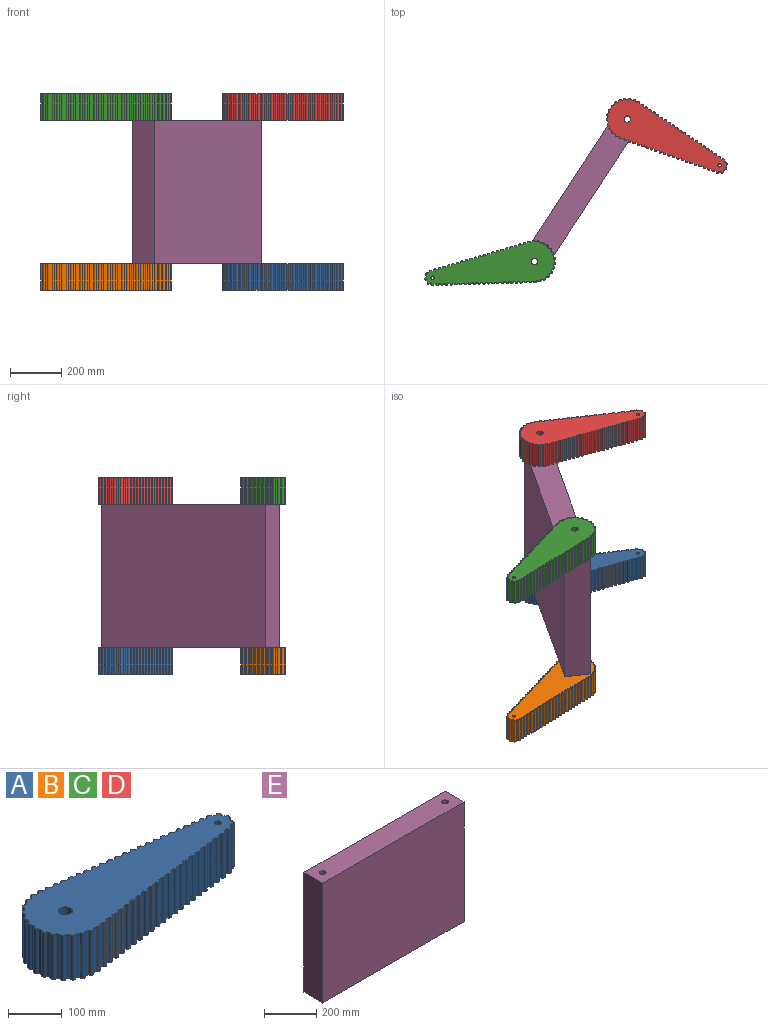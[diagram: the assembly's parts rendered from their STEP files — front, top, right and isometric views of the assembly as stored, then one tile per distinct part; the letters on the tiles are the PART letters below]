
ASSEMBLY  parts=5 mates=10
PART A: 128 faces, bbox 512.4x161.4x101.6 mm
  f0: plane 101.6x8.01mm, normal (0.13,-0.99,0), area 820.8mm2, adj f1,f124,f126,f127
  f1: cylinder r=5mm len=101.6mm, axis (0,0,-1), area 1595.9mm2, adj f0,f2,f126,f127
  f2: plane 101.6x8.01mm, normal (0.13,-0.99,0), area 820.8mm2, adj f1,f3,f126,f127
  f3: cylinder r=5mm len=101.6mm, axis (0,0,-1), area 1595.9mm2, adj f2,f4,f126,f127
  f4: plane 101.6x8.01mm, normal (0.13,-0.99,0), area 820.8mm2, adj f3,f5,f126,f127
  f5: cylinder r=5mm len=101.6mm, axis (0,0,-1), area 1595.9mm2, adj f4,f6,f126,f127
  f6: plane 101.6x8.01mm, normal (0.13,-0.99,0), area 820.8mm2, adj f5,f7,f126,f127
  f7: cylinder r=5mm len=101.6mm, axis (0,0,-1), area 1595.9mm2, adj f6,f8,f126,f127
  f8: plane 101.6x8.01mm, normal (0.13,-0.99,0), area 820.8mm2, adj f7,f9,f126,f127
  f9: cylinder r=5mm len=101.6mm, axis (0,0,-1), area 1595.9mm2, adj f8,f10,f126,f127
  f10: plane 101.6x8.01mm, normal (0.13,-0.99,0), area 820.8mm2, adj f9,f11,f126,f127
  f11: cylinder r=5mm len=101.6mm, axis (0,0,-1), area 1595.9mm2, adj f10,f12,f126,f127
  f12: plane 101.6x8.01mm, normal (0.13,-0.99,0), area 820.8mm2, adj f11,f13,f126,f127
  f13: cylinder r=5mm len=101.6mm, axis (0,0,-1), area 1595.9mm2, adj f12,f14,f126,f127
  f14: plane 101.6x8.01mm, normal (0.13,-0.99,0), area 820.8mm2, adj f13,f15,f126,f127
  f15: cylinder r=5mm len=101.6mm, axis (0,0,-1), area 1595.9mm2, adj f14,f16,f126,f127
  f16: plane 101.6x8.01mm, normal (0.13,-0.99,0), area 820.8mm2, adj f15,f17,f126,f127
  f17: cylinder r=5mm len=101.6mm, axis (0,0,-1), area 1595.9mm2, adj f16,f18,f126,f127
  f18: plane 101.6x8.01mm, normal (0.13,-0.99,0), area 820.8mm2, adj f17,f19,f126,f127
  f19: cylinder r=5mm len=101.6mm, axis (0,0,-1), area 1595.9mm2, adj f18,f20,f126,f127
  f20: plane 101.6x8.01mm, normal (0.13,-0.99,0), area 820.8mm2, adj f19,f21,f126,f127
  f21: cylinder r=5mm len=101.6mm, axis (0,0,-1), area 1595.9mm2, adj f20,f22,f126,f127
  f22: plane 101.6x8.01mm, normal (0.13,-0.99,0), area 820.8mm2, adj f21,f23,f126,f127
  f23: cylinder r=5mm len=101.6mm, axis (0,0,-1), area 1595.9mm2, adj f22,f24,f126,f127
  f24: plane 101.6x8.01mm, normal (0.13,-0.99,0), area 820.8mm2, adj f23,f25,f126,f127
  f25: cylinder r=5mm len=101.6mm, axis (0,0,-1), area 1595.9mm2, adj f24,f26,f126,f127
  f26: plane 101.6x8.01mm, normal (0.13,-0.99,0), area 820.8mm2, adj f25,f27,f126,f127
  f27: cylinder r=5mm len=101.6mm, axis (0,0,-1), area 1595.9mm2, adj f26,f28,f126,f127
  f28: plane 101.6x8.01mm, normal (0.13,-0.99,0), area 820.8mm2, adj f27,f29,f126,f127
  f29: cylinder r=5mm len=101.6mm, axis (0,0,-1), area 1595.9mm2, adj f28,f30,f126,f127
  f30: plane 101.6x8.01mm, normal (0.13,-0.99,0), area 820.8mm2, adj f29,f31,f126,f127
  f31: cylinder r=5mm len=101.6mm, axis (0,0,-1), area 1595.9mm2, adj f30,f32,f126,f127
  f32: plane 101.6x8.01mm, normal (0.13,-0.99,0), area 820.8mm2, adj f31,f33,f126,f127
  f33: cylinder r=5mm len=101.6mm, axis (0,0,-1), area 1595.9mm2, adj f32,f34,f126,f127
  f34: plane 101.6x8.01mm, normal (0.13,-0.99,0), area 820.8mm2, adj f33,f35,f126,f127
  f35: cylinder r=5mm len=101.6mm, axis (0,0,-1), area 1595.9mm2, adj f34,f36,f126,f127
  f36: plane 101.6x8.01mm, normal (0.13,-0.99,0), area 820.8mm2, adj f35,f37,f126,f127
  f37: cylinder r=5mm len=101.6mm, axis (0,0,-1), area 1595.9mm2, adj f36,f38,f126,f127
  f38: plane 101.6x8.01mm, normal (0.13,-0.99,0), area 820.8mm2, adj f37,f39,f126,f127
  f39: cylinder r=5mm len=101.6mm, axis (0,0,-1), area 1595.9mm2, adj f38,f40,f126,f127
  f40: plane 101.6x8.01mm, normal (0.13,-0.99,0), area 820.8mm2, adj f39,f41,f126,f127
  f41: cylinder r=5mm len=101.6mm, axis (0,0,-1), area 1646.4mm2, adj f40,f42,f126,f127
  f42: cylinder r=25.19mm len=101.6mm, axis (0,0,-1), area 829.1mm2, adj f41,f43,f126,f127
  f43: cylinder r=5mm len=101.6mm, axis (0,0,-1), area 1696.9mm2, adj f42,f44,f126,f127
  f44: cylinder r=25.19mm len=101.6mm, axis (0,0,-1), area 829.1mm2, adj f43,f45,f126,f127
  f45: cylinder r=5mm len=101.6mm, axis (0,0,-1), area 1696.9mm2, adj f44,f46,f126,f127
  f46: cylinder r=25.19mm len=101.6mm, axis (0,0,-1), area 829.1mm2, adj f45,f47,f126,f127
  f47: cylinder r=5mm len=101.6mm, axis (0,0,-1), area 1696.9mm2, adj f46,f48,f126,f127
  f48: cylinder r=25.19mm len=101.6mm, axis (0,0,-1), area 829.1mm2, adj f47,f49,f126,f127
  f49: cylinder r=5mm len=101.6mm, axis (0,0,-1), area 1646.4mm2, adj f48,f50,f126,f127
  f50: plane 101.6x8.01mm, normal (0.13,0.99,0), area 820.8mm2, adj f49,f51,f126,f127
  f51: cylinder r=5mm len=101.6mm, axis (0,0,-1), area 1595.9mm2, adj f50,f52,f126,f127
  f52: plane 101.6x8.01mm, normal (0.13,0.99,0), area 820.8mm2, adj f51,f53,f126,f127
  f53: cylinder r=5mm len=101.6mm, axis (0,0,-1), area 1595.9mm2, adj f52,f54,f126,f127
  f54: plane 101.6x8.01mm, normal (0.13,0.99,0), area 820.8mm2, adj f53,f55,f126,f127
  f55: cylinder r=5mm len=101.6mm, axis (0,0,-1), area 1595.9mm2, adj f54,f56,f126,f127
  f56: plane 101.6x8.01mm, normal (0.13,0.99,0), area 820.8mm2, adj f55,f57,f126,f127
  f57: cylinder r=5mm len=101.6mm, axis (0,0,-1), area 1595.9mm2, adj f56,f58,f126,f127
  f58: plane 101.6x8.01mm, normal (0.13,0.99,0), area 820.8mm2, adj f57,f59,f126,f127
  f59: cylinder r=5mm len=101.6mm, axis (0,0,-1), area 1595.9mm2, adj f58,f60,f126,f127
  f60: plane 101.6x8.01mm, normal (0.13,0.99,0), area 820.8mm2, adj f59,f61,f126,f127
  f61: cylinder r=5mm len=101.6mm, axis (0,0,-1), area 1595.9mm2, adj f60,f62,f126,f127
  f62: plane 101.6x8.01mm, normal (0.13,0.99,0), area 820.8mm2, adj f61,f63,f126,f127
  f63: cylinder r=5mm len=101.6mm, axis (0,0,-1), area 1595.9mm2, adj f62,f64,f126,f127
  f64: plane 101.6x8.01mm, normal (0.13,0.99,0), area 820.8mm2, adj f63,f65,f126,f127
  f65: cylinder r=5mm len=101.6mm, axis (0,0,-1), area 1595.9mm2, adj f64,f66,f126,f127
  f66: plane 101.6x8.01mm, normal (0.13,0.99,0), area 820.8mm2, adj f65,f67,f126,f127
  f67: cylinder r=5mm len=101.6mm, axis (0,0,-1), area 1595.9mm2, adj f66,f68,f126,f127
  f68: plane 101.6x8.01mm, normal (0.13,0.99,0), area 820.8mm2, adj f67,f69,f126,f127
  f69: cylinder r=5mm len=101.6mm, axis (0,0,-1), area 1595.9mm2, adj f68,f70,f126,f127
  f70: plane 101.6x8.01mm, normal (0.13,0.99,0), area 820.8mm2, adj f69,f71,f126,f127
  f71: cylinder r=5mm len=101.6mm, axis (0,0,-1), area 1595.9mm2, adj f70,f72,f126,f127
  f72: plane 101.6x8.01mm, normal (0.13,0.99,0), area 820.8mm2, adj f71,f73,f126,f127
  f73: cylinder r=5mm len=101.6mm, axis (0,0,-1), area 1595.9mm2, adj f72,f74,f126,f127
  f74: plane 101.6x8.01mm, normal (0.13,0.99,0), area 820.8mm2, adj f73,f75,f126,f127
  f75: cylinder r=5mm len=101.6mm, axis (0,0,-1), area 1595.9mm2, adj f74,f76,f126,f127
  f76: plane 101.6x8.01mm, normal (0.13,0.99,0), area 820.8mm2, adj f75,f77,f126,f127
  f77: cylinder r=5mm len=101.6mm, axis (0,0,-1), area 1595.9mm2, adj f76,f78,f126,f127
  f78: plane 101.6x8.01mm, normal (0.13,0.99,0), area 820.8mm2, adj f77,f79,f126,f127
  f79: cylinder r=5mm len=101.6mm, axis (0,0,-1), area 1595.9mm2, adj f78,f80,f126,f127
  f80: plane 101.6x8.01mm, normal (0.13,0.99,0), area 820.8mm2, adj f79,f81,f126,f127
  f81: cylinder r=5mm len=101.6mm, axis (0,0,-1), area 1595.9mm2, adj f80,f82,f126,f127
  f82: plane 101.6x8.01mm, normal (0.13,0.99,0), area 820.8mm2, adj f81,f83,f126,f127
  f83: cylinder r=5mm len=101.6mm, axis (0,0,-1), area 1595.9mm2, adj f82,f84,f126,f127
  f84: plane 101.6x8.01mm, normal (0.13,0.99,0), area 820.8mm2, adj f83,f85,f126,f127
  f85: cylinder r=5mm len=101.6mm, axis (0,0,-1), area 1595.9mm2, adj f84,f86,f126,f127
  f86: plane 101.6x8.01mm, normal (0.13,0.99,0), area 820.8mm2, adj f85,f87,f126,f127
  f87: cylinder r=5mm len=101.6mm, axis (0,0,-1), area 1595.9mm2, adj f86,f88,f126,f127
  f88: plane 101.6x8.01mm, normal (0.13,0.99,0), area 820.8mm2, adj f87,f89,f126,f127
  f89: cylinder r=5mm len=101.6mm, axis (0,0,-1), area 1595.9mm2, adj f88,f90,f126,f127
  f90: plane 101.6x8.01mm, normal (0.13,0.99,0), area 820.8mm2, adj f89,f91,f126,f127
  f91: cylinder r=5mm len=101.6mm, axis (0,0,-1), area 1595.9mm2, adj f90,f92,f126,f127
  f92: plane 101.6x8.01mm, normal (0.13,0.99,0), area 820.8mm2, adj f91,f93,f126,f127
  f93: cylinder r=5mm len=101.6mm, axis (0,0,-1), area 1612.6mm2, adj f92,f94,f126,f127
  f94: cylinder r=76.2mm len=101.6mm, axis (0,0,-1), area 862.2mm2, adj f93,f95,f126,f127
  f95: cylinder r=5mm len=101.6mm, axis (0,0,-1), area 1629.3mm2, adj f94,f96,f126,f127
  f96: cylinder r=76.2mm len=101.6mm, axis (0,0,-1), area 862.2mm2, adj f95,f97,f126,f127
  f97: cylinder r=5mm len=101.6mm, axis (0,0,-1), area 1629.3mm2, adj f96,f98,f126,f127
  f98: cylinder r=76.2mm len=101.6mm, axis (0,0,-1), area 862.2mm2, adj f97,f99,f126,f127
  f99: cylinder r=5mm len=101.6mm, axis (0,0,-1), area 1629.3mm2, adj f98,f100,f126,f127
  f100: cylinder r=76.2mm len=101.6mm, axis (0,0,-1), area 862.2mm2, adj f99,f101,f126,f127
  f101: cylinder r=5mm len=101.6mm, axis (0,0,-1), area 1629.3mm2, adj f100,f102,f126,f127
  f102: cylinder r=76.2mm len=101.6mm, axis (0,0,-1), area 862.2mm2, adj f101,f103,f126,f127
  f103: cylinder r=5mm len=101.6mm, axis (0,0,-1), area 1629.3mm2, adj f102,f104,f126,f127
  f104: cylinder r=76.2mm len=101.6mm, axis (0,0,-1), area 862.2mm2, adj f103,f105,f126,f127
  f105: cylinder r=5mm len=101.6mm, axis (0,0,-1), area 1629.3mm2, adj f104,f106,f126,f127
  f106: cylinder r=76.2mm len=101.6mm, axis (0,0,-1), area 862.2mm2, adj f105,f107,f126,f127
  f107: cylinder r=5mm len=101.6mm, axis (0,0,-1), area 1629.3mm2, adj f106,f108,f126,f127
  f108: cylinder r=76.2mm len=101.6mm, axis (0,0,-1), area 862.2mm2, adj f107,f109,f126,f127
  f109: cylinder r=5mm len=101.6mm, axis (0,0,-1), area 1629.3mm2, adj f108,f110,f126,f127
  f110: cylinder r=76.2mm len=101.6mm, axis (0,0,-1), area 862.2mm2, adj f109,f111,f126,f127
  f111: cylinder r=5mm len=101.6mm, axis (0,0,-1), area 1629.3mm2, adj f110,f112,f126,f127
  f112: cylinder r=76.2mm len=101.6mm, axis (0,0,-1), area 862.2mm2, adj f111,f113,f126,f127
  f113: cylinder r=5mm len=101.6mm, axis (0,0,-1), area 1629.3mm2, adj f112,f114,f126,f127
  f114: cylinder r=76.2mm len=101.6mm, axis (0,0,-1), area 862.2mm2, adj f113,f115,f126,f127
  f115: cylinder r=5mm len=101.6mm, axis (0,0,-1), area 1629.3mm2, adj f114,f116,f126,f127
  f116: cylinder r=76.2mm len=101.6mm, axis (0,0,-1), area 862.2mm2, adj f115,f117,f126,f127
  f117: cylinder r=5mm len=101.6mm, axis (0,0,-1), area 1629.3mm2, adj f116,f118,f126,f127
  f118: cylinder r=76.2mm len=101.6mm, axis (0,0,-1), area 862.2mm2, adj f117,f119,f126,f127
  f119: cylinder r=5mm len=101.6mm, axis (0,0,-1), area 1629.3mm2, adj f118,f120,f126,f127
  f120: cylinder r=76.2mm len=101.6mm, axis (0,0,-1), area 862.2mm2, adj f119,f121,f126,f127
  f121: cylinder r=5mm len=101.6mm, axis (0,0,-1), area 1612.6mm2, adj f120,f122,f126,f127
  f122: plane 101.6x8.01mm, normal (0.13,-0.99,0), area 820.8mm2, adj f121,f124,f126,f127
  f123: cylinder r=6.35mm len=101.6mm, axis (0,0,-1), area 4053.7mm2, adj f126,f127
  f124: cylinder r=5mm len=101.6mm, axis (0,0,-1), area 1595.9mm2, adj f0,f122,f126,f127
  f125: cylinder r=12.7mm len=101.6mm, axis (0,0,-1), area 8107.3mm2, adj f126,f127
  f126: plane 512.38x161.39mm, normal (0,0,1), area 52918.3mm2, adj f0,f1,f2,f3,f4,f5,f6,f7
  f127: plane 512.38x161.39mm, normal (0,0,-1), area 52918.3mm2, adj f0,f1,f2,f3,f4,f5,f6,f7
PART B: same geometry as A
PART C: same geometry as A
PART D: same geometry as A
PART E: 8 faces, bbox 762x101.6x558.8 mm
  f0: plane 558.8x101.6mm, normal (1,0,0), area 56774.1mm2, adj f1,f3,f4,f5
  f1: plane 762x101.6mm, normal (0,0,1), area 76405.8mm2, adj f0,f2,f4,f5,f6,f7
  f2: plane 558.8x101.6mm, normal (-1,0,0), area 56774.1mm2, adj f1,f3,f4,f5
  f3: plane 762x101.6mm, normal (0,0,-1), area 76405.8mm2, adj f0,f2,f4,f5,f6,f7
  f4: plane 762x558.8mm, normal (0,-1,0), area 425805.6mm2, adj f0,f1,f2,f3
  f5: plane 762x558.8mm, normal (0,1,0), area 425805.6mm2, adj f0,f1,f2,f3
  f6: cylinder r=12.7mm len=558.8mm, axis (0,0,1), area 44590.3mm2, adj f1,f3
  f7: cylinder r=12.7mm len=558.8mm, axis (0,0,1), area 44590.3mm2, adj f1,f3
PLACE A rot(axis=(0,0,-1),26.7deg) t=(89.01,614.73,-807.95)mm
PLACE B rot(axis=(-0.08,1,0),180deg) t=(-272.1,61.81,-706.35)mm
PLACE C rot(axis=(-0.08,1,0),180deg) t=(-272.1,61.81,-45.95)mm fixed
PLACE D rot(axis=(0.97,-0.23,0),180deg) t=(89.01,614.73,-45.95)mm
PLACE E rot(axis=(0,0,1),56.9deg) t=(74.26,685.05,-45.95)mm
MATE cylindrical B.f46 <-> C.f46  axis (0,0,1) through (-668.15,-0.96,-757.15)mm
MATE planar D.f125 <-> E.f7  axis (0,0,-1) through (89.01,614.73,-147.55)mm
MATE cylindrical C.f125 <-> E.f6  axis (0,0,-1) through (-272.1,61.81,-147.55)mm
MATE planar C.f126 <-> E.f1  axis (0,0,-1) through (-408.46,40.2,-147.55)mm
MATE cylindrical D.f125 <-> E.f7  axis (0,0,-1) through (89.01,614.73,-147.55)mm
MATE cylindrical D.f46 <-> A.f46  axis (0,0,1) through (447.37,434.82,-96.75)mm
MATE planar A.f126 <-> E.f7  axis (0,0,1) through (212.39,552.79,-706.35)mm
MATE cylindrical A.f125 <-> E.f7  axis (0,0,1) through (89.01,614.73,-706.35)mm
MATE cylindrical B.f125 <-> E.f6  axis (0,0,1) through (-272.1,61.81,-706.35)mm
MATE planar B.f127 <-> E.f6  axis (0,0,1) through (-408.46,40.2,-706.35)mm
